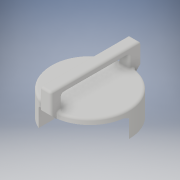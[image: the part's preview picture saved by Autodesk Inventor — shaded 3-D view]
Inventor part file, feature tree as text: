
AUTODESK INVENTOR PART (.ipt)
format: ipt  version: 2017 (Build 210142000, 142)  size: 316,416 bytes
history: native  units: in
note: dims shown in document units (in); Inventor stores cm internally (conversion verified against a paired STEP export)
features: projected_geometry x7, extrude x5, sketch x5, chamfer x4, fillet x1
ambient origin geometry x8: Origin, YZ Plane, XZ Plane, XY Plane, X Axis, Y Axis, Z Axis, Center Point
bodies: Solid1 (feature_tree)
feature tree (22):
  extrude  "Extrusion1"  Depth=0.1969in TaperAngle=0.0deg
  extrude  "Extrusion2"  Depth=0.5512in
  extrude  "Extrusion3"  Depth=1.5748in
  extrude  "Extrusion4"  Depth=1.5748in
  extrude  "Extrusion5"  Depth=0.0787in
  chamfer  "Chamfer1"  Distance=0.3937in
  chamfer  "Chamfer2"  Distance=0.7087in
  chamfer  "Chamfer3"  Distance=0.3937in
  chamfer  "Chamfer4"  Distance=0.2362in
  fillet  "Fillet1"  Radius=0.3937in
  sketch  "Sketch1"  dims[d0=2.7559in d1=0.1969in d2=0.0in]
  sketch  "Sketch2"  dims[d3=0.5512in d4=0.5512in]
  projected_geometry  "Projected Loop1"
  sketch  "Sketch3"  dims[d5=0.5512in d6=1.5748in]
  projected_geometry  "Projected Loop2"
  projected_geometry  "Projected Loop3"
  projected_geometry  "Projected Loop4"
  sketch  "Sketch4"  dims[d7=0.5512in d8=1.5748in]
  projected_geometry  "Projected Loop5"
  sketch  "Sketch5"  dims[d9=0.7087in d10=0.0in d11=3.1496in d12=0.3937in d13=0.7087in d14=0.0in d15=0.3937in d16=0.2362in d17=0.3937in d18=0.7087in d19=0.0in d20=45.0deg d21=45.0deg d22=0.7087in d23=0.0in d24=0.0787in d25=0.0787in d26=45.0deg d27=0.0787in d28=0.0787in d29=45.0deg d30=0.0787in d31=0.0787in d32=45.0deg d33=0.0787in d34=0.0787in d35=45.0deg d36=0.0787in]
  projected_geometry  "Projected Loop6"
  projected_geometry  "Projected Loop7"
